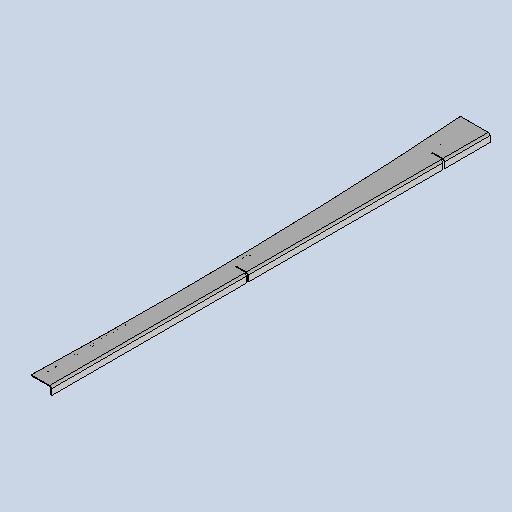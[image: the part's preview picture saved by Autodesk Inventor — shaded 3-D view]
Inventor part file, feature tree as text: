
AUTODESK INVENTOR PART (.ipt)
format: ipt  version: 2025 (Build 290162010, 162A)  size: 442,368 bytes
history: native  units: mm
features: sketch x6, other x5, sheet_metal_op x4, extrude x2, projected_geometry x2, chamfer x1, pattern_linear x1
ambient origin geometry x8: Origin, YZ Plane, XZ Plane, XY Plane, X Axis, Y Axis, Z Axis, Center Point
bodies: Body1 (feature_tree)
feature tree (21):
  sheet_metal_op  "Face2"
  sheet_metal_op  "Flange2"
  extrude  "Extrusion2"  Depth=6.0mm
  chamfer  "Chamfer2"  Distance=2.75mm
  pattern_linear  "Rectangular Pattern3"  Count1=2 Spacing1=90.0deg
  other  "Mark1"
  other  "A-Side Definition"
  extrude  "Extrusion3"  Depth=2.0mm
  sketch  "Sketch1"  dims[d16=1500.0mm d17=2700.0mm d18=2100.0mm d19=6.0mm d20=3.0mm d21=3.0mm d22=6.0mm d23=3.0mm d24=241.9mm d25=50.0mm d26=50.0mm d27=3.0mm d28=110.0mm d29=25.0mm d30=104.0mm d31=25.0mm d32=20.0mm d33=50.0mm d37=6.0mm d38=3.0mm d39=3.0mm]
  other  "Plate3"
  sketch  "Sketch3"  dims[d46=2.0mm]
  other  "Plate4"
  sheet_metal_op  "Bend2"
  sheet_metal_op  "Corner2"
  sketch  "Sketch5"  dims[d47=2.0mm]
  projected_geometry  "Projected Loop2"
  sketch  "Sketch Rectangular Pattern1"  dims[d43=3.0mm]
  sketch  "Sketch6"  dims[d48=1.0mm]
  sketch  "Sketch7"  dims[d49=4.0mm d50=2.75mm d51=20.0mm d52=90.0deg d53=2.75mm d54=8.0mm d55=2.0mm d56=2.75mm d57=500.0mm d58=500.0mm d59=500.0mm d60=500.0mm d61=500.0mm d69=1839.242466mm d70=2.0mm d71=0.0mm d72=0.0mm d76=67.563014mm d77=30.0mm d79=30.0mm d80=48.359031mm d81=30.0mm d83=250.0mm d84=40.0mm d86=550.0mm d87=10.0mm d89=10.0mm d91=274.556536mm d94=5.0mm d95=30.0mm d96=5.0mm d97=30.0mm d98=5.0mm d102=77.905549mm d104=51.799453mm d106=2.0mm d107=5.0mm d108=116.0mm d109=500.0mm d110=500.0mm d111=500.0mm d112=31.0mm d113=40.0mm d115=500.0mm d117=8.0mm d118=2.0mm d119=45.0deg d120=200.0mm d121=14.0mm d124=50.0mm d125=12.0mm d126=50.0mm d127=25.0mm d128=50.0mm d129=12.0mm d130=50.0mm d131=12.0mm d132=50.0mm d133=12.0mm d134=50.0mm d135=25.0mm d136=25.0mm d137=25.0mm d138=50.0mm d139=50.0mm d140=50.0mm d141=0.0mm d142=0.0mm d143=100.0mm]
  projected_geometry  "Projected Loop3"
  other  "Definition1"
